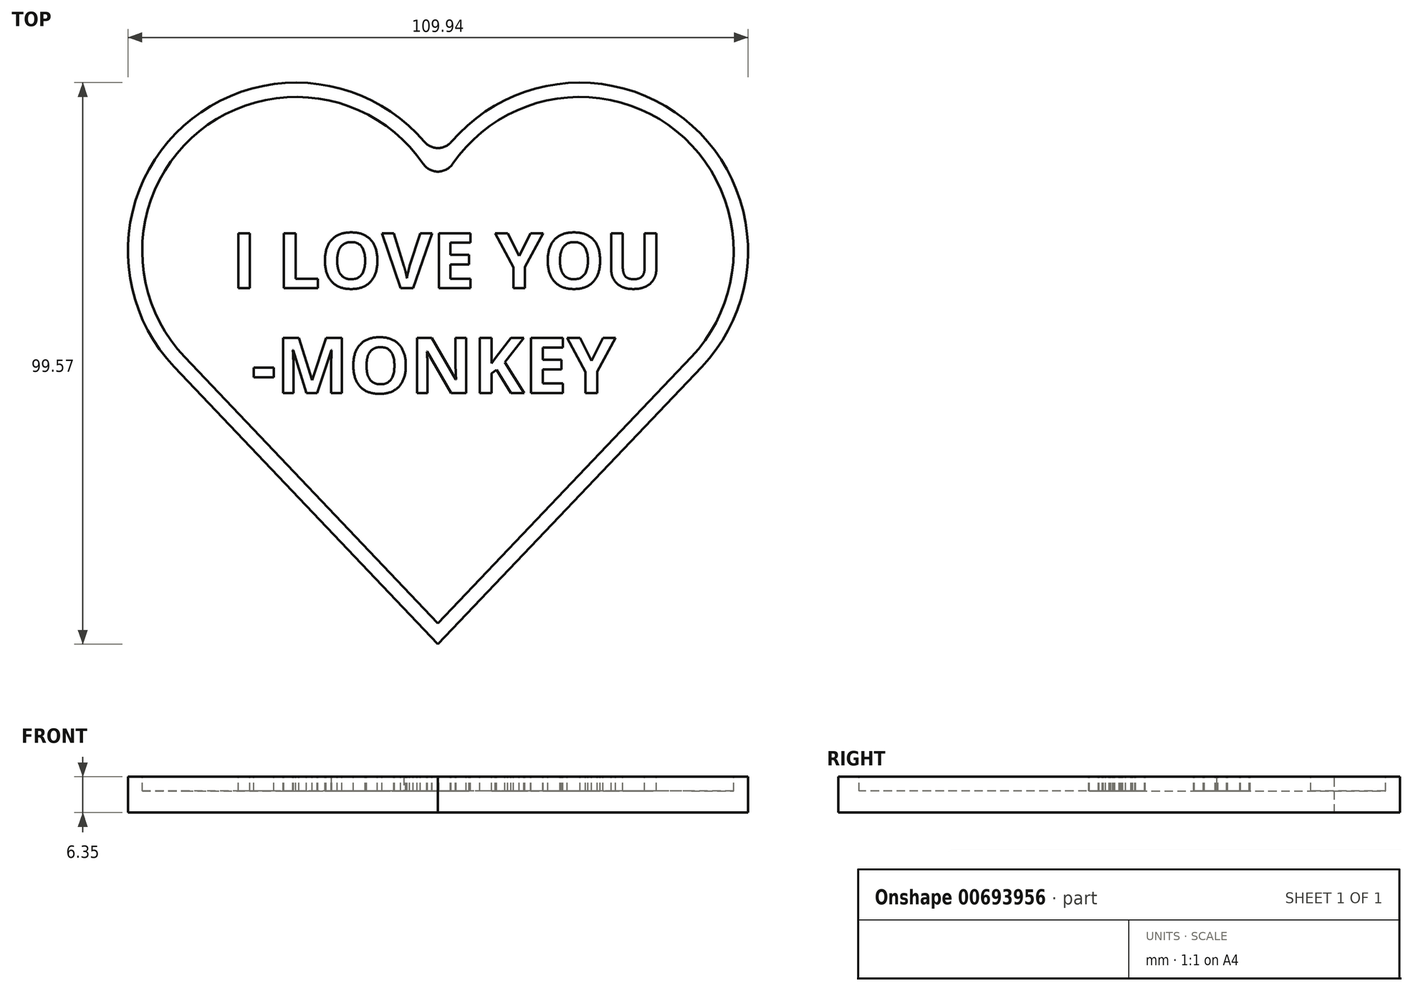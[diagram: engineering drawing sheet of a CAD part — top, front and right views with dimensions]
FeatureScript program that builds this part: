
annotation { "Feature Type Name" : "Feature", "Feature Type Description" : "" }
export const myFeature = defineFeature(function(context is Context, id is Id, definition is map)
    precondition{}
    {
        {
            var Q0;
            Q0=qCreatedBy(makeId("Top.planeOp"),FACE);
            var sketch = newSketch(context, id + "F0", { "sketchPlane" : qUnion([Q0])});
            skPoint(sketch, "E0.middle", {"position": v(0, 0) * mm});
            skArc(sketch, "E1", {"start": v(0, 36.46) * mm, "mid": v(-43.53, 43.86) * mm, "end": v(-46.75, -0.18) * mm});
            skLineSegment(sketch, "E2", {"start": v(-46.75, -0.18) * mm, "end": v(0, -49.36) * mm});
            skLineSegment(sketch, "E3", {"start": v(0, 55.2) * mm, "end": v(0, -57.46) * mm, "construction": true});
            skArc(sketch, "E4.MirrorCS", {"start": v(0, 36.46) * mm, "mid": v(43.53, 43.86) * mm, "end": v(46.75, -0.18) * mm});
            skLineSegment(sketch, "E5.MirrorCS", {"start": v(46.75, -0.18) * mm, "end": v(0, -49.36) * mm});
            skSolve(sketch);
        }
        {
            var Q0;
            Q0 = qSketchRegion(id + "F0", true);
            extrude(context, id + "F1", {"entities" : qUnion([Q0]), "depth" : 6.35 * mm, "offsetDistance" : 25.4 * mm});
        }
        {
            var Q0;
            Q0=makeQuery(id+"F1.opExtrude","CAP_FACE",FACE,{"disambiguationData":[OSD([sQuery(id+"F0.wireOp",EDGE,"E1"),sQuery(id+"F0.wireOp",EDGE,"E2"),sQuery(id+"F0.wireOp",EDGE,"E4.MirrorCS"),sQuery(id+"F0.wireOp",EDGE,"E5.MirrorCS")])],"isStart":false});
            var sketch = newSketch(context, id + "F2", { "sketchPlane" : qUnion([Q0])});
            skText(sketch, "E6", { "text": "I LOVE YOU\n -MONKEY", "fontName": "OpenSans-Bold.ttf"});
            const initialGuessF2  = {"E6": [-0.03646, 0.01372, 1, 0, 0.00984]};
            skSetInitialGuess(sketch, initialGuessF2);
            skSolve(sketch);
        }
        {
            var Q0;
            {var subQ0=sQuery(id+"F0.wireOp",EDGE,"E2");var subQ1=sQuery(id+"F0.wireOp",EDGE,"E5.MirrorCS");var subQ2=sQuery(id+"F0.wireOp",EDGE,"E1");var subQ3=sQuery(id+"F0.wireOp",EDGE,"E4.MirrorCS");Q0=makeQuery(id+"FENd4om5qOS4p4j_1.boolean.opBoolean","SPLIT",FACE,{"disambiguationData":[TD([makeQuery(id+"F1.opExtrude","SWEPT_FACE",FACE,{"disambiguationData":[OSD([subQ2])]})])],"derivedFrom":makeQuery(id+"F1.opExtrude","CAP_FACE",FACE,{"disambiguationData":[OSD([subQ2,subQ0,subQ3,subQ1])],"isStart":false})});}
            var sketch = newSketch(context, id + "F3", { "sketchPlane" : qUnion([Q0])});
            skArc(sketch, "E7.0", {"start": v(0, 31.03) * mm, "mid": v(-40.1, 43.2) * mm, "end": v(-44.91, 1.57) * mm});
            skArc(sketch, "E7.1", {"start": v(0, 31.03) * mm, "mid": v(40.1, 43.2) * mm, "end": v(44.91, 1.57) * mm});
            skLineSegment(sketch, "E7.2", {"start": v(44.91, 1.57) * mm, "end": v(0, -45.68) * mm});
            skLineSegment(sketch, "E7.3", {"start": v(-44.91, 1.57) * mm, "end": v(0, -45.68) * mm});
            skText(sketch, "E8", { "text": "I LOVE YOU\n -MONKEY", "fontName": "OpenSans-Bold.ttf"});
            const initialGuessF3  = {"E8": [-0.03662, 0.01375, 1, 0, 0.00984]};
            skSetInitialGuess(sketch, initialGuessF3);
            skSolve(sketch);
        }
        {
            var Q0;
            Q0=makeQuery(id+"F3.imprint","IMPRINT",FACE,{"disambiguationData":[TD([[makeQuery(id+"F3.imprint","IMPRINT",EDGE,{"derivedFrom":sQuery(id+"F3.wireOp",EDGE,"E8.sketch_text.stroke-18")}),1.0]])]});
            var Q1;
            Q1=makeQuery(id+"F3.imprint","IMPRINT",FACE,{"disambiguationData":[TD([[makeQuery(id+"F3.imprint","IMPRINT",EDGE,{"derivedFrom":sQuery(id+"F3.wireOp",EDGE,"E8.sketch_text.stroke-63")}),1.0]])]});
            var Q2;
            Q2=makeQuery(id+"F3.imprint","IMPRINT",FACE,{"disambiguationData":[TD([[makeQuery(id+"F3.imprint","IMPRINT",EDGE,{"derivedFrom":sQuery(id+"F3.wireOp",EDGE,"E7.0")}),1.0]])]});
            var Q3;
            Q3=makeQuery(id+"F2.imprint","IMPRINT",FACE,{"disambiguationData":[TD([[makeQuery(id+"F2.imprint","IMPRINT",EDGE,{"derivedFrom":sQuery(id+"F2.wireOp",EDGE,"E6.sketch_text.stroke-115")}),1.0]])]});
            extrude(context, id + "F4", {"entities" : qUnion([Q0, Q1, Q2, Q3]), "operationType" : NewBodyOperationType.REMOVE, "oppositeDirection" : true, "depth" : 2.54 * mm, "offsetDistance" : 25.4 * mm});
        }
        {
            var Q0;
            Q0=makeQuery(id+"F1.opExtrude","SWEPT_EDGE",EDGE,{"disambiguationData":[OSD([sQuery(id+"F0.wireOp",EDGE,"E1"),sQuery(id+"F0.wireOp",EDGE,"E4.MirrorCS")])]});
            var Q1;
            Q1=makeQuery(id+"F4.boolean.opBoolean","COPY",EDGE,{"derivedFrom":makeQuery(id+"F4.opExtrude","SWEPT_EDGE",EDGE,{"disambiguationData":[OSD([sQuery(id+"F3.wireOp",EDGE,"E7.0"),sQuery(id+"F3.wireOp",EDGE,"E7.1")])]})});
            fillet(context, id + "F5", {"entities" : qUnion([Q0, Q1]), "radius" : 3.17 * mm, "tangentPropagation" : true, "allowEdgeOverflow" : false});
        }
    });
